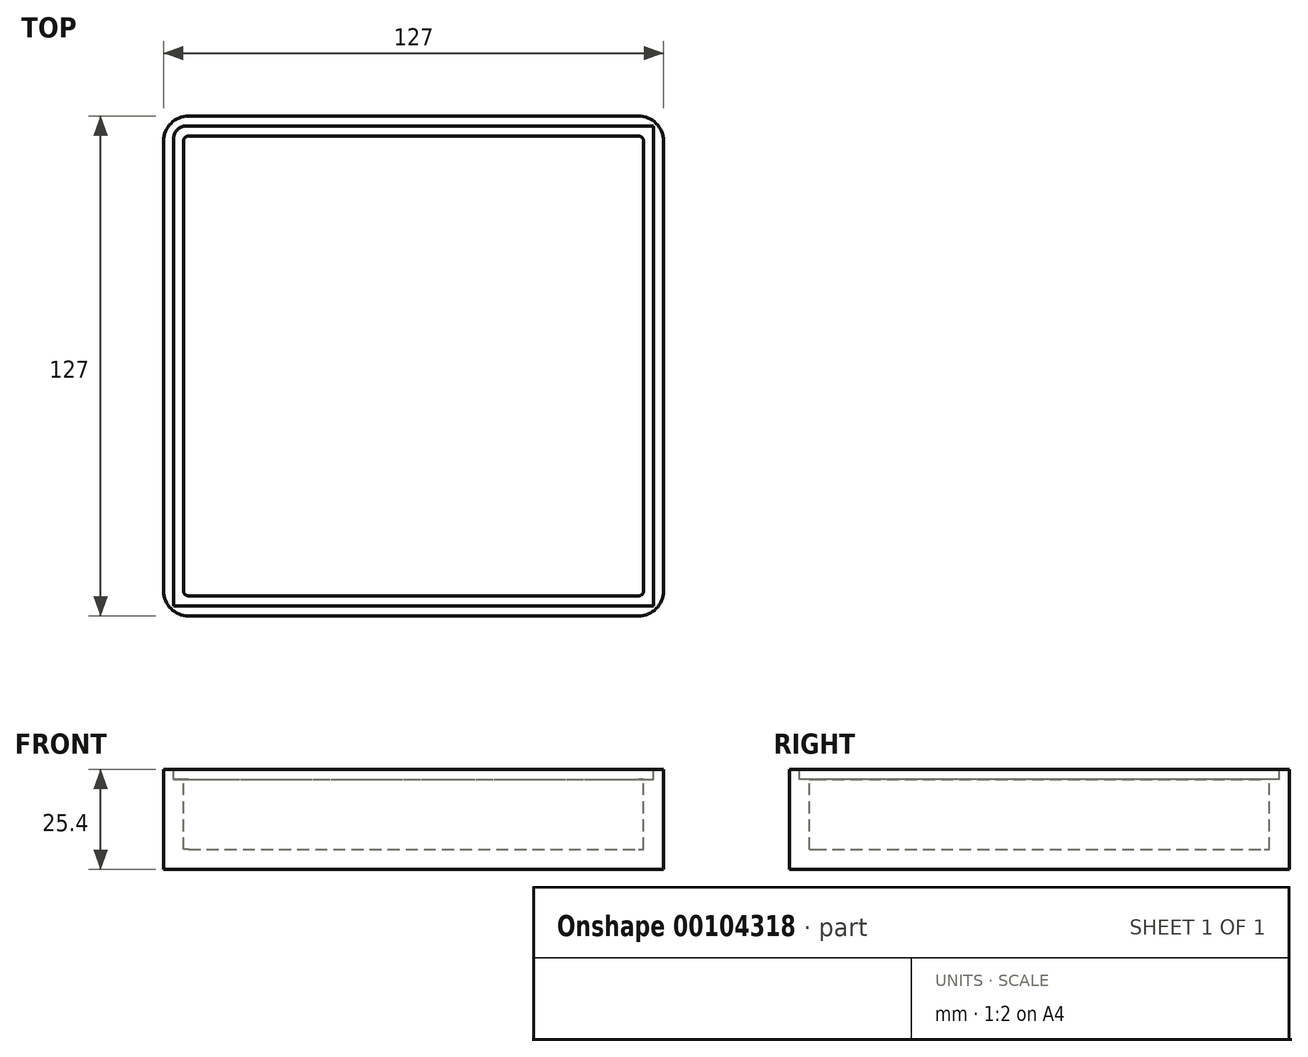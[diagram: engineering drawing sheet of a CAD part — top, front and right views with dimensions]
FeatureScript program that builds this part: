
annotation { "Feature Type Name" : "Feature", "Feature Type Description" : "" }
export const myFeature = defineFeature(function(context is Context, id is Id, definition is map)
    precondition{}
    {
        {
            var Q0;
            Q0=qCreatedBy(makeId("Top.planeOp"),FACE);
            var sketch = newSketch(context, id + "F0", { "sketchPlane" : qUnion([Q0])});
            skLineSegment(sketch, "E0.bottom", {"start": v(-63.5, -63.5) * mm, "end": v(63.5, -63.5) * mm});
            skLineSegment(sketch, "E0.top", {"start": v(-63.5, 63.5) * mm, "end": v(63.5, 63.5) * mm});
            skLineSegment(sketch, "E0.left", {"start": v(-63.5, -63.5) * mm, "end": v(-63.5, 63.5) * mm});
            skLineSegment(sketch, "E0.right", {"start": v(63.5, -63.5) * mm, "end": v(63.5, 63.5) * mm});
            skPoint(sketch, "E0.middle", {"position": v(0, 0) * mm});
            skSolve(sketch);
        }
        {
            var Q0;
            Q0 = qSketchRegion(id + "F0", true);
            extrude(context, id + "F1", {"entities" : qUnion([Q0]), "depth" : 25.4 * mm});
        }
        {
            var Q0;
            Q0=makeQuery(id+"F1.opExtrude","SWEPT_EDGE",EDGE,{"disambiguationData":[OSD([sQuery(id+"F0.wireOp",EDGE,"E0.bottom"),sQuery(id+"F0.wireOp",EDGE,"E0.right")])]});
            var Q1;
            Q1=makeQuery(id+"F1.opExtrude","SWEPT_EDGE",EDGE,{"disambiguationData":[OSD([sQuery(id+"F0.wireOp",EDGE,"E0.top"),sQuery(id+"F0.wireOp",EDGE,"E0.right")])]});
            var Q2;
            Q2=makeQuery(id+"F1.opExtrude","SWEPT_EDGE",EDGE,{"disambiguationData":[OSD([sQuery(id+"F0.wireOp",EDGE,"E0.top"),sQuery(id+"F0.wireOp",EDGE,"E0.left")])]});
            var Q3;
            Q3=makeQuery(id+"F1.opExtrude","SWEPT_EDGE",EDGE,{"disambiguationData":[OSD([sQuery(id+"F0.wireOp",EDGE,"E0.bottom"),sQuery(id+"F0.wireOp",EDGE,"E0.left")])]});
            fillet(context, id + "F2", {"entities" : qUnion([Q0, Q1, Q2, Q3]), "radius" : 6.35 * mm, "tangentPropagation" : true, "allowEdgeOverflow" : false});
        }
        {
            var Q0;
            Q0=makeQuery(id+"F1.opExtrude","CAP_FACE",FACE,{"disambiguationData":[OSD([sQuery(id+"F0.wireOp",EDGE,"E0.bottom"),sQuery(id+"F0.wireOp",EDGE,"E0.top"),sQuery(id+"F0.wireOp",EDGE,"E0.left"),sQuery(id+"F0.wireOp",EDGE,"E0.right")])],"isStart":false});
            shell(context, id + "F3", {"entities" : qUnion([Q0]), "thickness" : 5.08 * mm});
        }
        {
            var Q0;
            Q0=makeQuery(id+"F1.opExtrude","CAP_FACE",FACE,{"disambiguationData":[OSD([sQuery(id+"F0.wireOp",EDGE,"E0.bottom"),sQuery(id+"F0.wireOp",EDGE,"E0.top"),sQuery(id+"F0.wireOp",EDGE,"E0.left"),sQuery(id+"F0.wireOp",EDGE,"E0.right")])],"isStart":false});
            var sketch = newSketch(context, id + "F4", { "sketchPlane" : qUnion([Q0])});
            skLineSegment(sketch, "E1.bottom", {"start": v(-57.78, 60.96) * mm, "end": v(60.96, 60.96) * mm});
            skLineSegment(sketch, "E1.top", {"start": v(-60.96, -60.96) * mm, "end": v(60.96, -60.96) * mm});
            skLineSegment(sketch, "E1.left", {"start": v(-60.96, 57.79) * mm, "end": v(-60.96, -60.96) * mm});
            skLineSegment(sketch, "E1.right", {"start": v(60.96, 60.96) * mm, "end": v(60.96, -60.96) * mm});
            skPoint(sketch, "E1.middle", {"position": v(0, 0) * mm});
            skPoint(sketch, "E2.visualSharp", {"position": v(-60.96, 60.96) * mm});
            skArc(sketch, "E2.filletArc", {"start": v(-57.78, 60.96) * mm, "mid": v(-60.03, 60.03) * mm, "end": v(-60.96, 57.79) * mm});
            skSolve(sketch);
        }
        {
            var Q0;
            Q0 = qSketchRegion(id + "F4", true);
            extrude(context, id + "F5", {"entities" : qUnion([Q0]), "operationType" : NewBodyOperationType.REMOVE, "oppositeDirection" : true, "depth" : 2.54 * mm});
        }
    });
